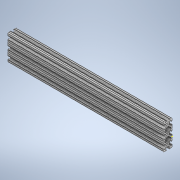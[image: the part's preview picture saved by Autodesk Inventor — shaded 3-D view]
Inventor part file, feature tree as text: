
AUTODESK INVENTOR PART (.ipt)
format: ipt  version: 2020 (Build 240168000, 168)  size: 375,296 bytes
history: native  units: in
note: dims shown in document units (in); Inventor stores cm internally (conversion verified against a paired STEP export)
features: sketch x2, extrude x1
ambient origin geometry x8: Origin, YZ Plane, XZ Plane, XY Plane, X Axis, Y Axis, Z Axis, Center Point
bodies: Solid1 (feature_tree)
feature tree (3):
  extrude  "Extrusion1"  [1 undecoded]
  sketch  "Sketch2"
  sketch  "Sketch1"  dims[d0=18.0in d1=0.0in]
note: 1 required parameter value undecoded (feature->parameter linkage not recoverable at this tier; creation-order binding heuristic only, values carry confidence <= 0.55)
